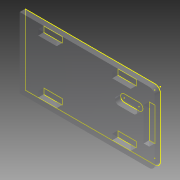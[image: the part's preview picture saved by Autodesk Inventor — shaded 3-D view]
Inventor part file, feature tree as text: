
AUTODESK INVENTOR PART (.ipt)
format: ipt  version: 2015 (Build 190159000, 159)  size: 168,448 bytes
history: native  units: mm
features: sketch x3, extrude x2, projected_geometry x2, fillet x1
ambient origin geometry x8: Origin, YZ Plane, XZ Plane, XY Plane, X Axis, Y Axis, Z Axis, Center Point
bodies: Solid1 (feature_tree)
feature tree (8):
  extrude  "Extrusion1"  Depth=38.0mm
  fillet  "Fillet1"  Radius=3.0mm
  extrude  "Extrusion2"  Depth=3.0mm
  sketch  "Sketch3"  dims[d6=10.0mm d7=10.0mm d8=18.0mm d9=32.0mm d10=3.0mm d11=3.0mm d12=3.0mm d13=10.0mm d14=13.0mm d15=3.0mm d16=0.0mm d17=3.0mm d21=2.0mm d22=8.0mm d23=11.5mm d24=3.0mm d25=0.0mm d26=15.0mm]
  sketch  "Sketch1"  dims[d0=73.0mm d1=38.0mm d3=3.0mm]
  sketch  "Sketch2"  dims[d4=3.0mm d5=3.0mm]
  projected_geometry  "Projected Loop1"
  projected_geometry  "Projected Loop2"
